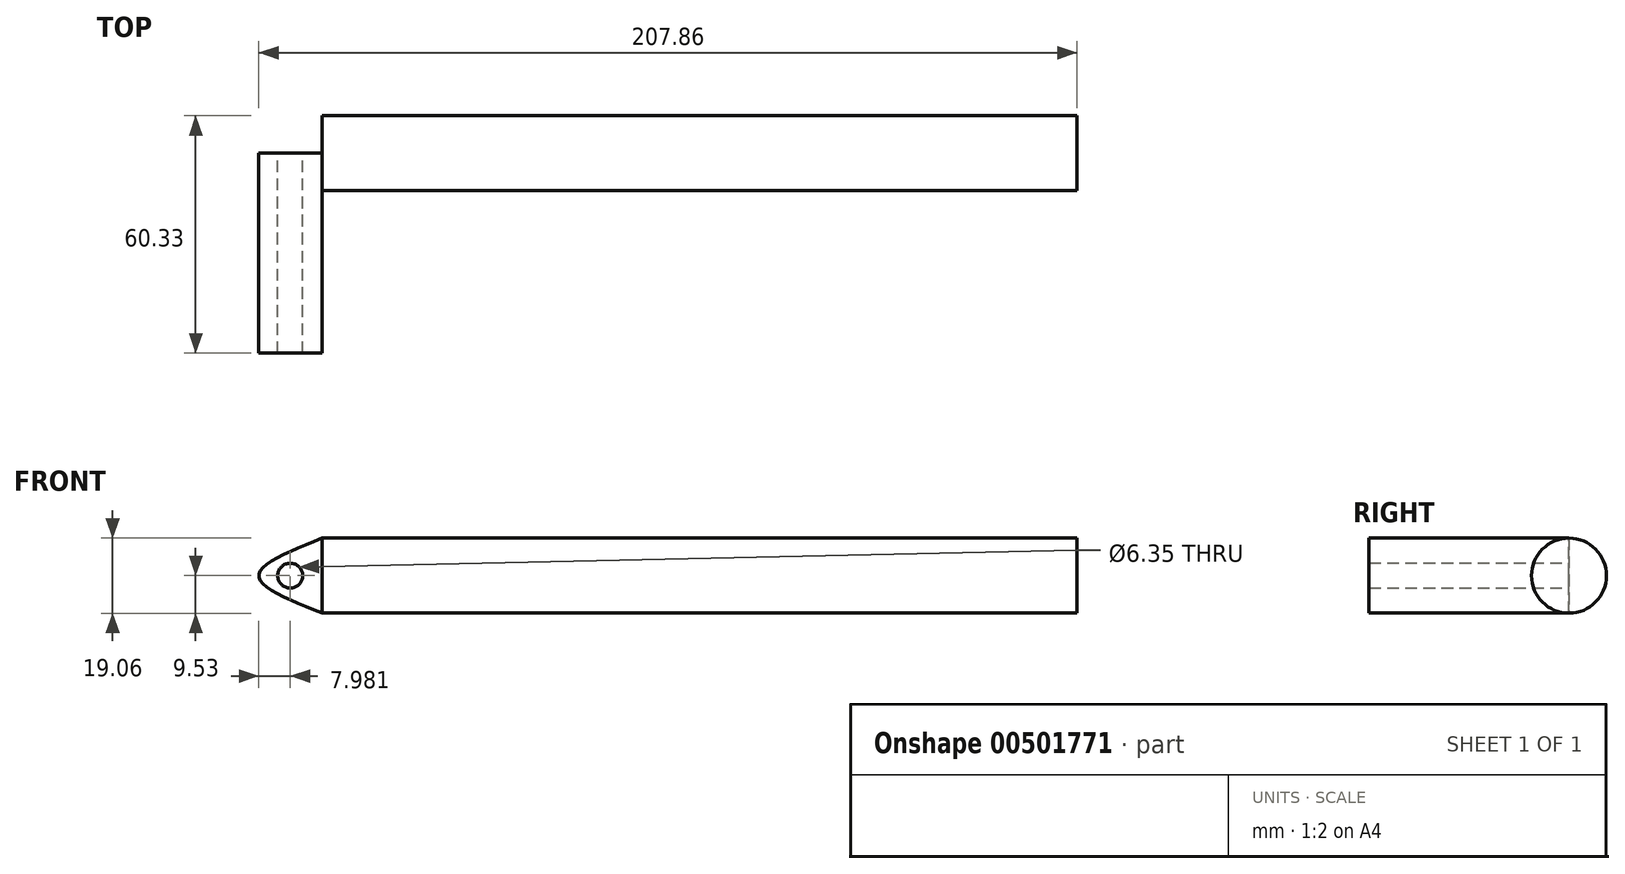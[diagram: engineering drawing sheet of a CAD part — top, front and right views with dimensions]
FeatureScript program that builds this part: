
annotation { "Feature Type Name" : "Feature", "Feature Type Description" : "" }
export const myFeature = defineFeature(function(context is Context, id is Id, definition is map)
    precondition{}
    {
        {
            var Q0;
            Q0=qCreatedBy(makeId("Right.planeOp"),FACE);
            var sketch = newSketch(context, id + "F0", { "sketchPlane" : qUnion([Q0])});
            skCircle(sketch, "E0", {"center": v(0, 0) * mm, "radius": 9.53 * mm});
            skSolve(sketch);
        }
        {
            var Q0;
            Q0 = qSketchRegion(id + "F0", true);
            extrude(context, id + "F1", {"entities" : qUnion([Q0]), "endBound" : BoundingType.SYMMETRIC, "depth" : 115.57 * mm});
        }
        {
            var Q0;
            Q0=qCreatedBy(makeId("Front.planeOp"),FACE);
            var sketch = newSketch(context, id + "F2", { "sketchPlane" : qUnion([Q0])});
            skLineSegment(sketch, "E1", {"start": v(-57.79, 0) * mm, "end": v(-57.79, 9.52) * mm});
            skLineSegment(sketch, "E2", {"start": v(-57.79, 9.52) * mm, "end": v(-57.79, -9.53) * mm});
            skPoint(sketch, "E2.endSnap0", {"position": v(-57.79, 4.76) * mm});
            skFitSpline(sketch, "E3", {"points": [v(-57.79, -9.53) * mm, v(-73.87, 0) * mm, v(-57.79, 9.52) * mm], "startDerivative": vector(-48.26, 19.05) * mm, "endDerivative": vector(48.26, 19.05) * mm});
            skCircle(sketch, "E4", {"center": v(-65.89, 0) * mm, "radius": 3.18 * mm});
            skSolve(sketch);
        }
        {
            var Q0;
            Q0 = qSketchRegion(id + "F2", true);
            extrude(context, id + "F3", {"entities" : qUnion([Q0]), "operationType" : NewBodyOperationType.ADD, "depth" : 50.8 * mm});
        }
        {
            var Q0;
            Q0=makeQuery(id+"F1.opExtrude","CAP_FACE",FACE,{"disambiguationData":[OSD([sQuery(id+"F0.wireOp",EDGE,"E0")])],"isStart":false});
            var sketch = newSketch(context, id + "F4", { "sketchPlane" : qUnion([Q0])});
            skCircle(sketch, "E5", {"center": v(0, 0) * mm, "radius": 9.53 * mm});
            skSolve(sketch);
        }
        {
            var Q0;
            Q0 = qSketchRegion(id + "F4", true);
            extrude(context, id + "F5", {"entities" : qUnion([Q0]), "operationType" : NewBodyOperationType.ADD, "depth" : 76.2 * mm});
        }
    });
